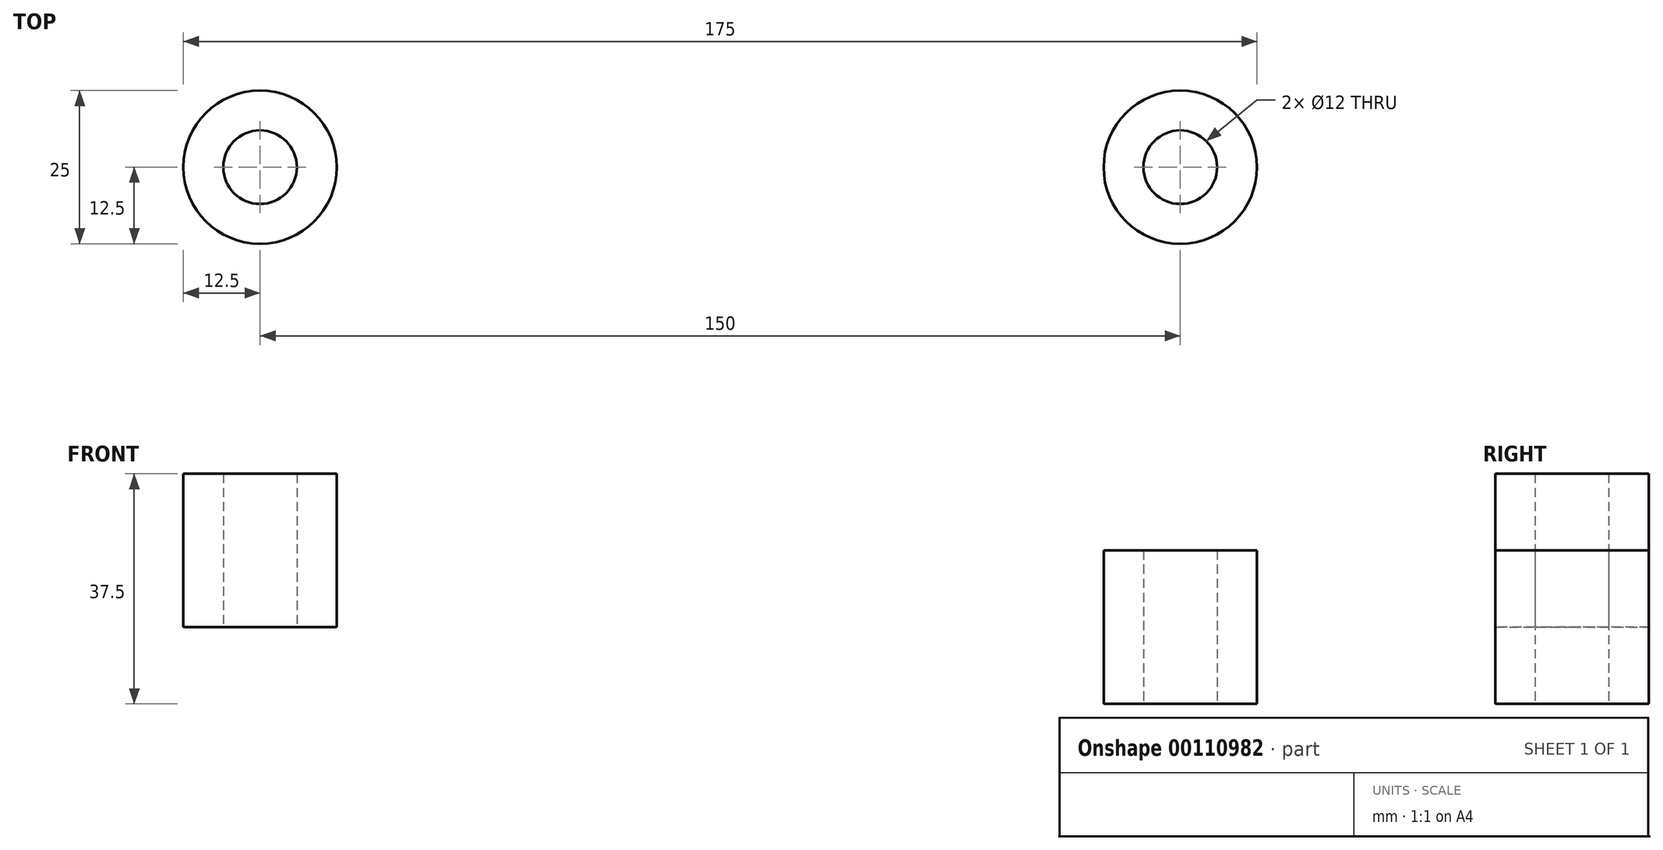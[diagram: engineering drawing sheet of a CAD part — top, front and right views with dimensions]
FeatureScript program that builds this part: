
annotation { "Feature Type Name" : "Feature", "Feature Type Description" : "" }
export const myFeature = defineFeature(function(context is Context, id is Id, definition is map)
    precondition{}
    {
        {
            var Q0;
            Q0=qCreatedBy(makeId("Top.planeOp"),FACE);
            var sketch = newSketch(context, id + "F0", { "sketchPlane" : qUnion([Q0])});
            skCircle(sketch, "E0", {"center": v(0, 0) * mm, "radius": 12.5 * mm});
            skCircle(sketch, "E1", {"center": v(0, 0) * mm, "radius": 6 * mm});
            skLineSegment(sketch, "E2", {"start": v(0, 0) * mm, "end": v(150, 0) * mm, "construction": true});
            skCircle(sketch, "E3", {"center": v(150, 0) * mm, "radius": 12.5 * mm});
            skCircle(sketch, "E4", {"center": v(150, 0) * mm, "radius": 6 * mm});
            skSolve(sketch);
        }
        {
            var Q0;
            Q0=makeQuery(id+"F0.imprint","IMPRINT",FACE,{"disambiguationData":[TD([[makeQuery(id+"F0.imprint","IMPRINT",EDGE,{"derivedFrom":sQuery(id+"F0.wireOp",EDGE,"E0")}),1.0]])]});
            extrude(context, id + "F1", {"entities" : qUnion([Q0]), "depth" : 25 * mm});
        }
        {
            var Q0;
            Q0=makeQuery(id+"F0.imprint","IMPRINT",FACE,{"disambiguationData":[TD([[makeQuery(id+"F0.imprint","IMPRINT",EDGE,{"derivedFrom":sQuery(id+"F0.wireOp",EDGE,"E3")}),1.0]])]});
            extrude(context, id + "F2", {"entities" : qUnion([Q0]), "endBound" : BoundingType.SYMMETRIC, "depth" : 25 * mm});
        }
    });
